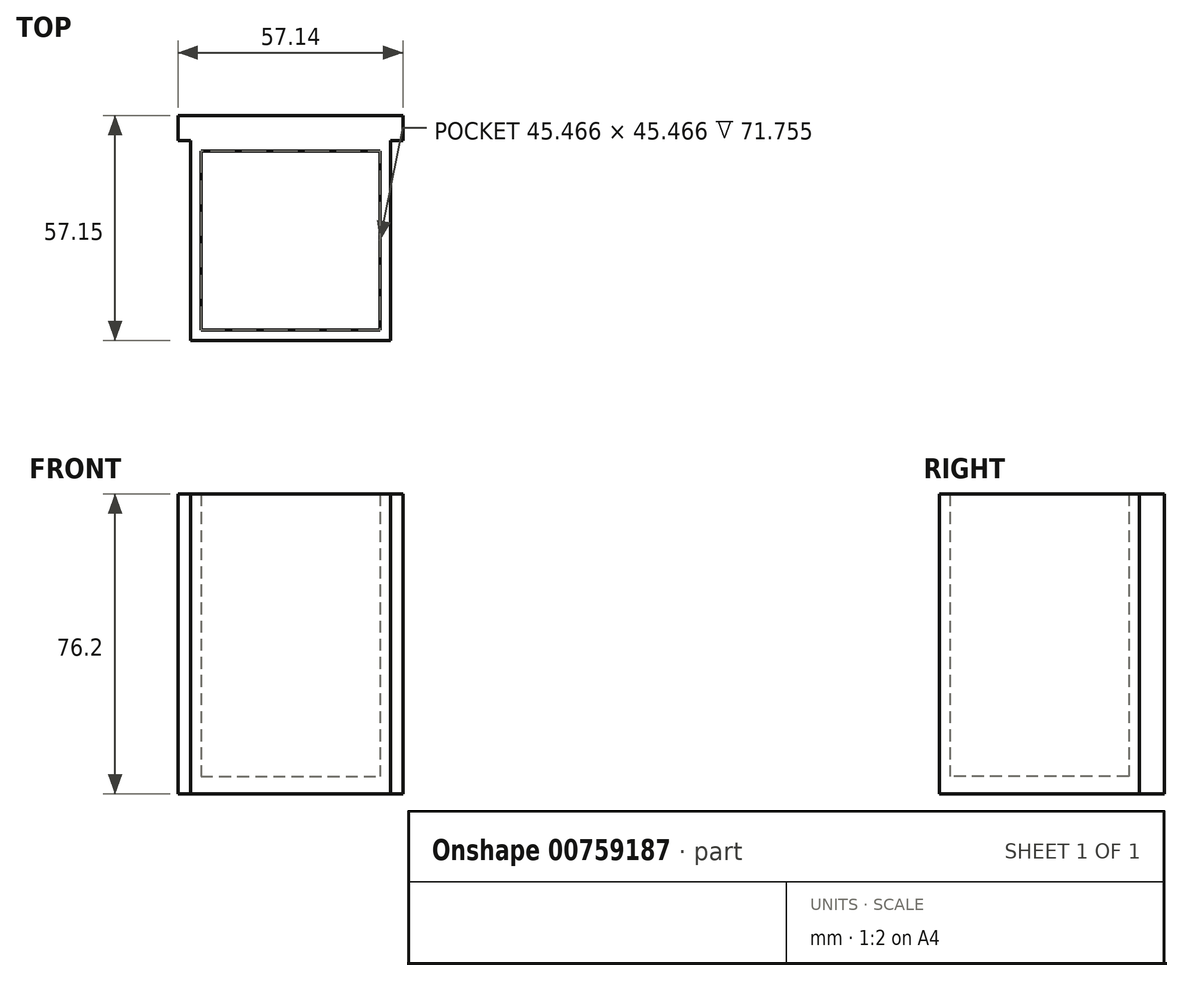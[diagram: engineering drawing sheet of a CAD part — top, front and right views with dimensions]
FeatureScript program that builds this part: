
annotation { "Feature Type Name" : "Feature", "Feature Type Description" : "" }
export const myFeature = defineFeature(function(context is Context, id is Id, definition is map)
    precondition{}
    {
        {
            var Q0;
            Q0=qCreatedBy(makeId("Front.planeOp"),FACE);
            var sketch = newSketch(context, id + "F0", { "sketchPlane" : qUnion([Q0])});
            skLineSegment(sketch, "E0.bottom", {"start": v(28.57, 38.1) * mm, "end": v(-28.58, 38.1) * mm});
            skLineSegment(sketch, "E0.top", {"start": v(28.58, -38.1) * mm, "end": v(-28.57, -38.1) * mm});
            skLineSegment(sketch, "E0.left", {"start": v(28.57, 38.1) * mm, "end": v(28.58, -38.1) * mm});
            skLineSegment(sketch, "E0.right", {"start": v(-28.58, 38.1) * mm, "end": v(-28.57, -38.1) * mm});
            skPoint(sketch, "E0.middle", {"position": v(0, 0) * mm});
            skSolve(sketch);
        }
        {
            var Q0;
            Q0=qCreatedBy(makeId("Top.planeOp"),FACE);
            var sketch = newSketch(context, id + "F1", { "sketchPlane" : qUnion([Q0])});
            skLineSegment(sketch, "E1.bottom", {"start": v(-25.4, 0) * mm, "end": v(25.4, 0) * mm});
            skLineSegment(sketch, "E1.top", {"start": v(-25.4, -50.8) * mm, "end": v(25.4, -50.8) * mm});
            skLineSegment(sketch, "E1.left", {"start": v(-25.4, 0) * mm, "end": v(-25.4, -50.8) * mm});
            skLineSegment(sketch, "E1.right", {"start": v(25.4, 0) * mm, "end": v(25.4, -50.8) * mm});
            skLineSegment(sketch, "E2.bottom", {"start": v(-22.73, -2.67) * mm, "end": v(22.73, -2.67) * mm});
            skLineSegment(sketch, "E2.top", {"start": v(-22.73, -48.13) * mm, "end": v(22.73, -48.13) * mm});
            skLineSegment(sketch, "E2.left", {"start": v(-22.73, -2.67) * mm, "end": v(-22.73, -48.13) * mm});
            skLineSegment(sketch, "E2.right", {"start": v(22.73, -2.67) * mm, "end": v(22.73, -48.13) * mm});
            skSolve(sketch);
        }
        {
            var Q0;
            Q0=makeQuery(id+"F0.imprint","IMPRINT",FACE,{"disambiguationData":[TD([[makeQuery(id+"F0.imprint","IMPRINT",EDGE,{"derivedFrom":sQuery(id+"F0.wireOp",EDGE,"E0.bottom")}),1.0]])]});
            extrude(context, id + "F2", {"entities" : qUnion([Q0]), "oppositeDirection" : true, "depth" : 6.35 * mm, "offsetDistance" : 25.4 * mm});
        }
        {
            var Q0;
            {var subQ0=sQuery(id+"F1.wireOp",EDGE,"E1.left");Q0=makeQuery(id+"F1.imprint","IMPRINT",FACE,{"disambiguationData":[TD([[makeQuery(id+"F1.imprint","IMPRINT",EDGE,{"derivedFrom":subQ0}),1.0]])]});}
            var Q1;
            {var subQ0=sQuery(id+"F1.wireOp",EDGE,"E1.right");Q1=makeQuery(id+"F1.imprint","IMPRINT",FACE,{"disambiguationData":[TD([[makeQuery(id+"F1.imprint","IMPRINT",EDGE,{"derivedFrom":subQ0}),-1.0]])]});}
            extrude(context, id + "F3", {"entities" : qUnion([Q0, Q1]), "operationType" : NewBodyOperationType.ADD, "endBound" : BoundingType.SYMMETRIC, "depth" : 76.2 * mm, "offsetDistance" : 25.4 * mm});
        }
        {
            var Q0;
            Q0=makeQuery(id+"F1.imprint","IMPRINT",FACE,{"disambiguationData":[TD([[makeQuery(id+"F1.imprint","IMPRINT",EDGE,{"derivedFrom":sQuery(id+"F1.wireOp",EDGE,"E2.bottom")}),-1.0]])]});
            var Q1;
            Q1=makeQuery(id+"F1.imprint","IMPRINT",FACE,{"disambiguationData":[TD([[makeQuery(id+"F1.imprint","IMPRINT",EDGE,{"derivedFrom":sQuery(id+"F1.wireOp",EDGE,"Rq2NiCl3-WjmO-C6gQ-4fG7-Q6qpqAbxgPdN.bottom")}),-1.0]])]});
            extrude(context, id + "F4", {"entities" : qUnion([Q0, Q1]), "operationType" : NewBodyOperationType.ADD, "oppositeDirection" : true, "depth" : 38.1 * mm, "offsetDistance" : 25.4 * mm, "hasSecondDirection" : true, "secondDirectionOppositeDirection" : true, "secondDirectionDepth" : 33.65 * mm});
        }
    });
